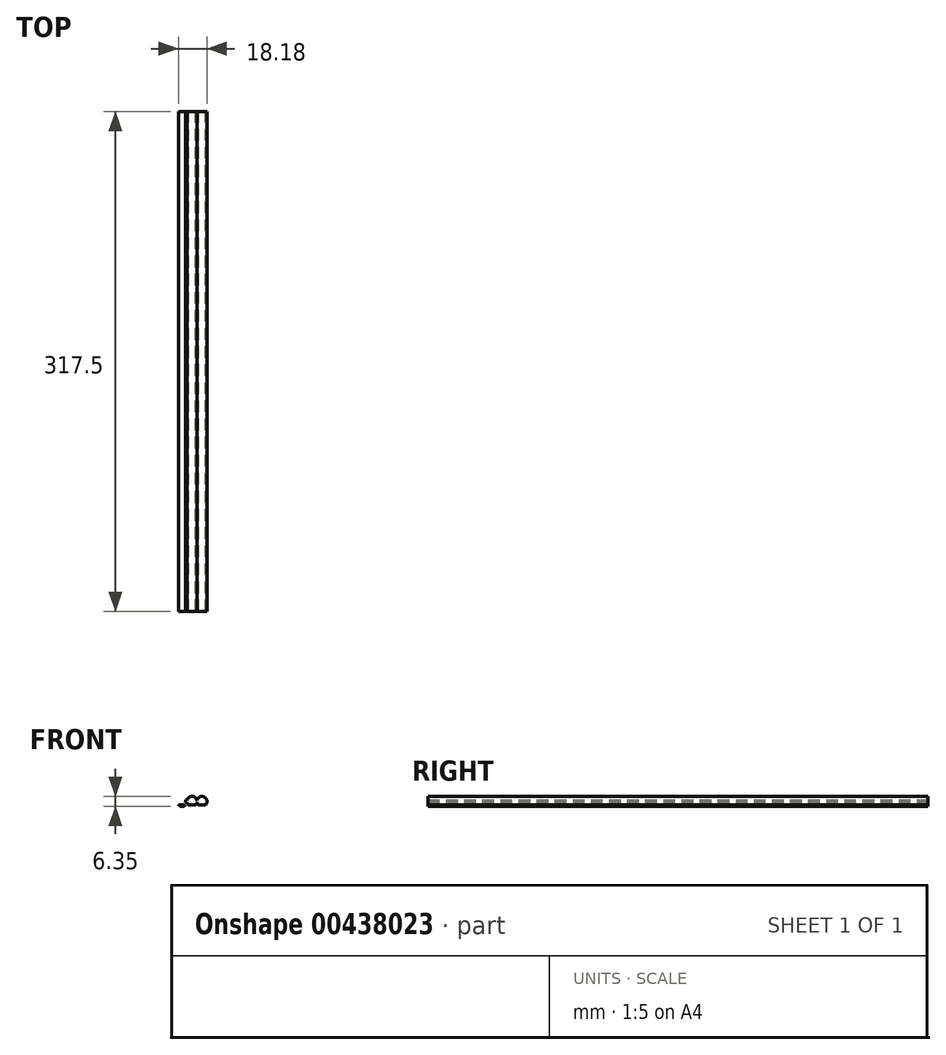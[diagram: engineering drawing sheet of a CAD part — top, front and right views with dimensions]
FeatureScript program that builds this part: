
annotation { "Feature Type Name" : "Feature", "Feature Type Description" : "" }
export const myFeature = defineFeature(function(context is Context, id is Id, definition is map)
    precondition{}
    {
        {
            var Q0;
            Q0=qCreatedBy(makeId("Front.planeOp"),FACE);
            var sketch = newSketch(context, id + "F0", { "sketchPlane" : qUnion([Q0])});
            skCircle(sketch, "E0", {"center": v(0, 0) * mm, "radius": 3.18 * mm});
            skLineSegment(sketch, "E1", {"start": v(-2.3, -2.2) * mm, "end": v(2.3, -2.2) * mm});
            skCircle(sketch, "E2", {"center": v(6.35, 0) * mm, "radius": 3.18 * mm});
            skCircle(sketch, "E3", {"center": v(12.7, 0) * mm, "radius": 3.18 * mm});
            skLineSegment(sketch, "E4", {"start": v(-2.3, -2.2) * mm, "end": v(15, -2.2) * mm});
            skLineSegment(sketch, "E5.bottom", {"start": v(2.34, 0.83) * mm, "end": v(4.02, 0.83) * mm});
            skLineSegment(sketch, "E5.top", {"start": v(2.34, -0.78) * mm, "end": v(4.02, -0.78) * mm});
            skLineSegment(sketch, "E5.left", {"start": v(2.34, 0.83) * mm, "end": v(2.34, -0.78) * mm});
            skLineSegment(sketch, "E5.right", {"start": v(4.02, 0.83) * mm, "end": v(4.02, -0.78) * mm});
            skLineSegment(sketch, "E6.bottom", {"start": v(9, 0.64) * mm, "end": v(10.28, 0.64) * mm});
            skLineSegment(sketch, "E6.top", {"start": v(9, -0.6) * mm, "end": v(10.28, -0.6) * mm});
            skLineSegment(sketch, "E6.left", {"start": v(9, 0.64) * mm, "end": v(9, -0.6) * mm});
            skLineSegment(sketch, "E6.right", {"start": v(10.28, 0.64) * mm, "end": v(10.28, -0.6) * mm});
            skSolve(sketch);
        }
        {
            var Q0;
            {var subQ0=sQuery(id+"F0.wireOp",EDGE,"E4");var subQ1=sQuery(id+"F0.wireOp",EDGE,"E0");var subQ2=makeQuery(id+"F0.imprint","INTERSECT",VERTEX,{"disambiguationData":[OD(0.0)],"derivedFrom":[subQ1,subQ0]});Q0=makeQuery(id+"F0.imprint","IMPRINT",FACE,{"disambiguationData":[TD([[makeQuery(id+"F0.imprint","IMPRINT",EDGE,{"disambiguationData":[TD([[subQ2,1.0]])],"derivedFrom":subQ1}),1.0]])]});}
            var Q1;
            {var subQ0=sQuery(id+"F0.wireOp",EDGE,"E2");var subQ1=makeQuery(id+"F0.imprint","INTERSECT",VERTEX,{"derivedFrom":[sQuery(id+"F0.wireOp",EDGE,"E0"),subQ0]});Q1=makeQuery(id+"F0.imprint","IMPRINT",FACE,{"disambiguationData":[TD([[makeQuery(id+"F0.imprint","IMPRINT",EDGE,{"disambiguationData":[TD([[subQ1,1.0]])],"derivedFrom":subQ0}),1.0]])]});}
            var Q2;
            {var subQ0=sQuery(id+"F0.wireOp",EDGE,"E5.left");Q2=makeQuery(id+"F0.imprint","IMPRINT",FACE,{"disambiguationData":[TD([[makeQuery(id+"F0.imprint","IMPRINT",EDGE,{"derivedFrom":subQ0}),1.0]])]});}
            var Q3;
            {var subQ0=sQuery(id+"F0.wireOp",EDGE,"E5.bottom");var subQ1=sQuery(id+"F0.wireOp",EDGE,"E0");var subQ2=makeQuery(id+"F0.imprint","INTERSECT",VERTEX,{"derivedFrom":[subQ1,subQ0]});Q3=makeQuery(id+"F0.imprint","IMPRINT",FACE,{"disambiguationData":[TD([[makeQuery(id+"F0.imprint","IMPRINT",EDGE,{"disambiguationData":[TD([[subQ2,1.0]])],"derivedFrom":subQ1}),-1.0]])]});}
            var Q4;
            {var subQ0=sQuery(id+"F0.wireOp",EDGE,"E2");var subQ1=sQuery(id+"F0.wireOp",EDGE,"E0");var subQ2=makeQuery(id+"F0.imprint","INTERSECT",VERTEX,{"derivedFrom":[subQ1,subQ0]});Q4=makeQuery(id+"F0.imprint","IMPRINT",FACE,{"disambiguationData":[TD([[makeQuery(id+"F0.imprint","IMPRINT",EDGE,{"disambiguationData":[TD([[subQ2,1.0]])],"derivedFrom":subQ1}),-1.0]])]});}
            var Q5;
            {var subQ13=sQuery(id+"F0.wireOp",EDGE,"E5.right");Q5=makeQuery(id+"F0.imprint","IMPRINT",FACE,{"disambiguationData":[TD([[makeQuery(id+"F0.imprint","IMPRINT",EDGE,{"derivedFrom":subQ13}),1.0]])]});}
            var Q6;
            {var subQ0=sQuery(id+"F0.wireOp",EDGE,"E6.left");Q6=makeQuery(id+"F0.imprint","IMPRINT",FACE,{"disambiguationData":[TD([[makeQuery(id+"F0.imprint","IMPRINT",EDGE,{"derivedFrom":subQ0}),1.0]])]});}
            var Q7;
            {var subQ4=sQuery(id+"F0.wireOp",EDGE,"E6.right");Q7=makeQuery(id+"F0.imprint","IMPRINT",FACE,{"disambiguationData":[TD([[makeQuery(id+"F0.imprint","IMPRINT",EDGE,{"derivedFrom":subQ4}),1.0]])]});}
            var Q8;
            {var subQ0=sQuery(id+"F0.wireOp",EDGE,"E6.right");Q8=makeQuery(id+"F0.imprint","IMPRINT",FACE,{"disambiguationData":[TD([[makeQuery(id+"F0.imprint","IMPRINT",EDGE,{"derivedFrom":subQ0}),-1.0]])]});}
            var Q9;
            {var subQ0=sQuery(id+"F0.wireOp",EDGE,"E6.bottom");var subQ1=sQuery(id+"F0.wireOp",EDGE,"E2");var subQ2=makeQuery(id+"F0.imprint","INTERSECT",VERTEX,{"derivedFrom":[subQ1,subQ0]});Q9=makeQuery(id+"F0.imprint","IMPRINT",FACE,{"disambiguationData":[TD([[makeQuery(id+"F0.imprint","IMPRINT",EDGE,{"disambiguationData":[TD([[subQ2,1.0]])],"derivedFrom":subQ1}),-1.0]])]});}
            var Q10;
            {var subQ0=sQuery(id+"F0.wireOp",EDGE,"E3");var subQ1=sQuery(id+"F0.wireOp",EDGE,"E2");var subQ2=makeQuery(id+"F0.imprint","INTERSECT",VERTEX,{"derivedFrom":[subQ1,subQ0]});Q10=makeQuery(id+"F0.imprint","IMPRINT",FACE,{"disambiguationData":[TD([[makeQuery(id+"F0.imprint","IMPRINT",EDGE,{"disambiguationData":[TD([[subQ2,1.0]])],"derivedFrom":subQ1}),-1.0]])]});}
            extrude(context, id + "F1", {"entities" : qUnion([Q0, Q1, Q2, Q3, Q4, Q5, Q6, Q7, Q8, Q9, Q10]), "depth" : 317.5 * mm});
        }
    });
